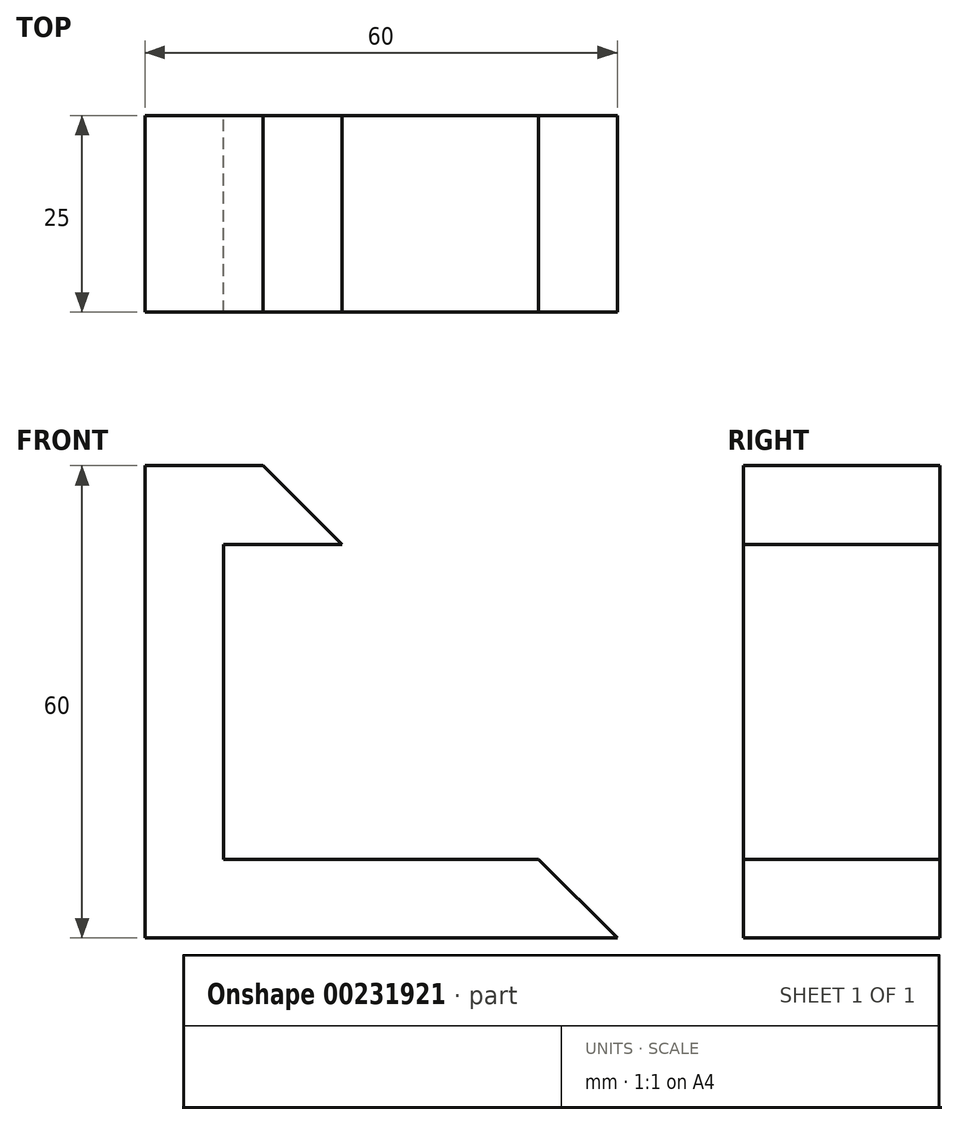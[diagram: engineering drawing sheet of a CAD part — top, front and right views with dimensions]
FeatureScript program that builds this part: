
annotation { "Feature Type Name" : "Feature", "Feature Type Description" : "" }
export const myFeature = defineFeature(function(context is Context, id is Id, definition is map)
    precondition{}
    {
        {
            var Q0;
            Q0=qCreatedBy(makeId("Front.planeOp"),FACE);
            var sketch = newSketch(context, id + "F0", { "sketchPlane" : qUnion([Q0])});
            skLineSegment(sketch, "E0", {"start": v(-60, 60) * mm, "end": v(-60, 0) * mm});
            skLineSegment(sketch, "E1", {"start": v(-60, 0) * mm, "end": v(0, 0) * mm});
            skLineSegment(sketch, "E2", {"start": v(0, 0) * mm, "end": v(-10, 10) * mm});
            skLineSegment(sketch, "E3", {"start": v(-10, 10) * mm, "end": v(-50, 10) * mm});
            skLineSegment(sketch, "E4", {"start": v(-50, 10) * mm, "end": v(-50, 50) * mm});
            skLineSegment(sketch, "E5", {"start": v(-50, 50) * mm, "end": v(-35, 50) * mm});
            skLineSegment(sketch, "E6", {"start": v(-35, 50) * mm, "end": v(-45, 60) * mm});
            skLineSegment(sketch, "E7", {"start": v(-45, 60) * mm, "end": v(-60, 60) * mm});
            skSolve(sketch);
        }
        {
            var Q0;
            Q0=makeQuery(id+"F0.imprint","IMPRINT",FACE,{"disambiguationData":[TD([[makeQuery(id+"F0.imprint","IMPRINT",EDGE,{"derivedFrom":sQuery(id+"F0.wireOp",EDGE,"E0")}),1.0]])]});
            extrude(context, id + "F1", {"entities" : qUnion([Q0]), "depth" : 25 * mm});
        }
    });
